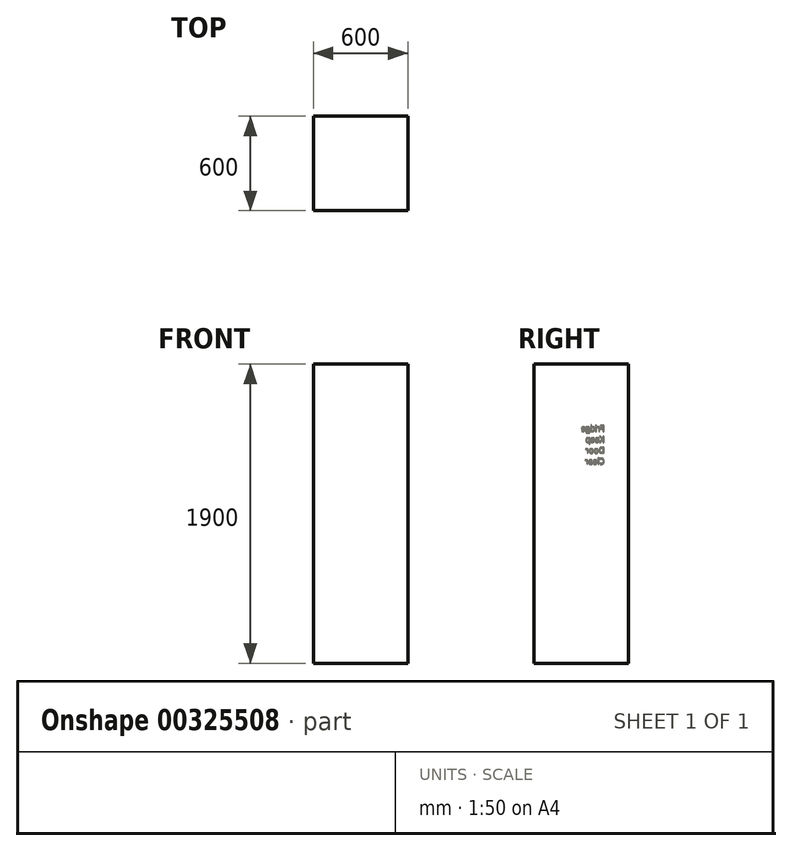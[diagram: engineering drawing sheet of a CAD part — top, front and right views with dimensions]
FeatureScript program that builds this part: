
annotation { "Feature Type Name" : "Feature", "Feature Type Description" : "" }
export const myFeature = defineFeature(function(context is Context, id is Id, definition is map)
    precondition{}
    {
        {
            var Q0;
            Q0=qCreatedBy(makeId("Top.planeOp"),FACE);
            var sketch = newSketch(context, id + "F0", { "sketchPlane" : qUnion([Q0])});
            skLineSegment(sketch, "E0.bottom", {"start": v(300, -300) * mm, "end": v(-300, -300) * mm});
            skLineSegment(sketch, "E0.top", {"start": v(300, 300) * mm, "end": v(-300, 300) * mm});
            skLineSegment(sketch, "E0.left", {"start": v(300, -300) * mm, "end": v(300, 300) * mm});
            skLineSegment(sketch, "E0.right", {"start": v(-300, -300) * mm, "end": v(-300, 300) * mm});
            skPoint(sketch, "E0.middle", {"position": v(0, 0) * mm});
            skSolve(sketch);
        }
        {
            var Q0;
            Q0 = qSketchRegion(id + "F0", true);
            extrude(context, id + "F1", {"entities" : qUnion([Q0]), "depth" : 1900 * mm});
        }
        {
            var Q0;
            Q0=makeQuery(id+"F1.opExtrude","SWEPT_FACE",FACE,{"disambiguationData":[OSD([sQuery(id+"F0.wireOp",EDGE,"E0.right")])]});
            var sketch = newSketch(context, id + "F2", { "sketchPlane" : qUnion([Q0])});
            skText(sketch, "E1", { "text": "Fridge\nKeep\nDoor\nClear", "fontName": "OpenSans-Regular.ttf"});
            const initialGuessF2  = {"E1": [-0.14917, 1.47385, 1, 0, 0.03689]};
            skSetInitialGuess(sketch, initialGuessF2);
            skSolve(sketch);
        }
        {
            var Q0;
            Q0 = qSketchRegion(id + "F2", true);
            extrude(context, id + "F3", {"entities" : qUnion([Q0]), "operationType" : NewBodyOperationType.REMOVE, "oppositeDirection" : true, "depth" : 5 * mm});
        }
    });
